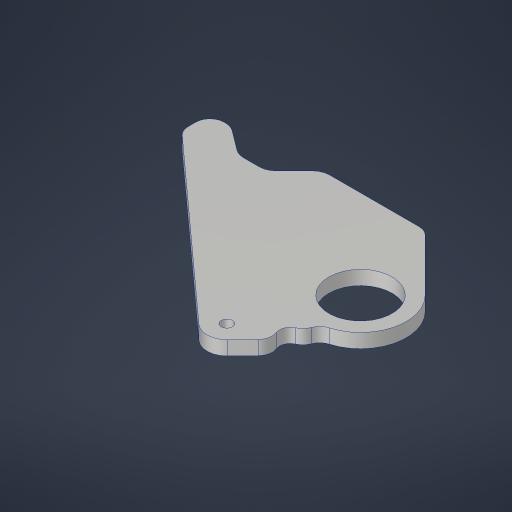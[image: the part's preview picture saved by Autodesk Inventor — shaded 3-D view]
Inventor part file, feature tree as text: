
AUTODESK INVENTOR PART (.ipt)
format: ipt  version: 2023.4 (Build 274418000, 418)  size: 231,424 bytes
history: native  units: in
note: dims shown in document units (in); Inventor stores cm internally (conversion verified against a paired STEP export)
features: fillet x2, sketch x1, extrude x1, hole x1
ambient origin geometry x8: Origin, YZ Plane, XZ Plane, XY Plane, X Axis, Y Axis, Z Axis, Center Point
bodies: Solid1 (feature_tree)
feature tree (5):
  sketch  "Sketch1"  dims[d0=1.315in d1=1.125in d2=0.25in d3=0.375in d4=1.25in d5=0.201in d6=0.25in d7=0.75in d8=0.375in d9=1.0in d10=1.0in d11=0.5in d12=0.5in d13=0.5in d15=3.0in d16=3.0in d17=0.5in d18=0.125in d19=0.375in d20=0.5in d23=0.25in d24=0.0in d25=0.25in d26=0.3in d27=0.201in d28=0.75in d29=0.385in d30=0.25in d31=0.5635in d32=1.0in d33=0.8108in d34=0.175in d35=0.05in d36=0.05in]
  extrude  "Extrusion1"  Depth=0.25in
  fillet  "Fillet1"  Radius=0.25in
  fillet  "Fillet2"  Radius=0.375in
  hole  "Hole1"  [1 undecoded]
note: 1 required parameter value undecoded (feature->parameter linkage not recoverable at this tier; creation-order binding heuristic only, values carry confidence <= 0.55)
